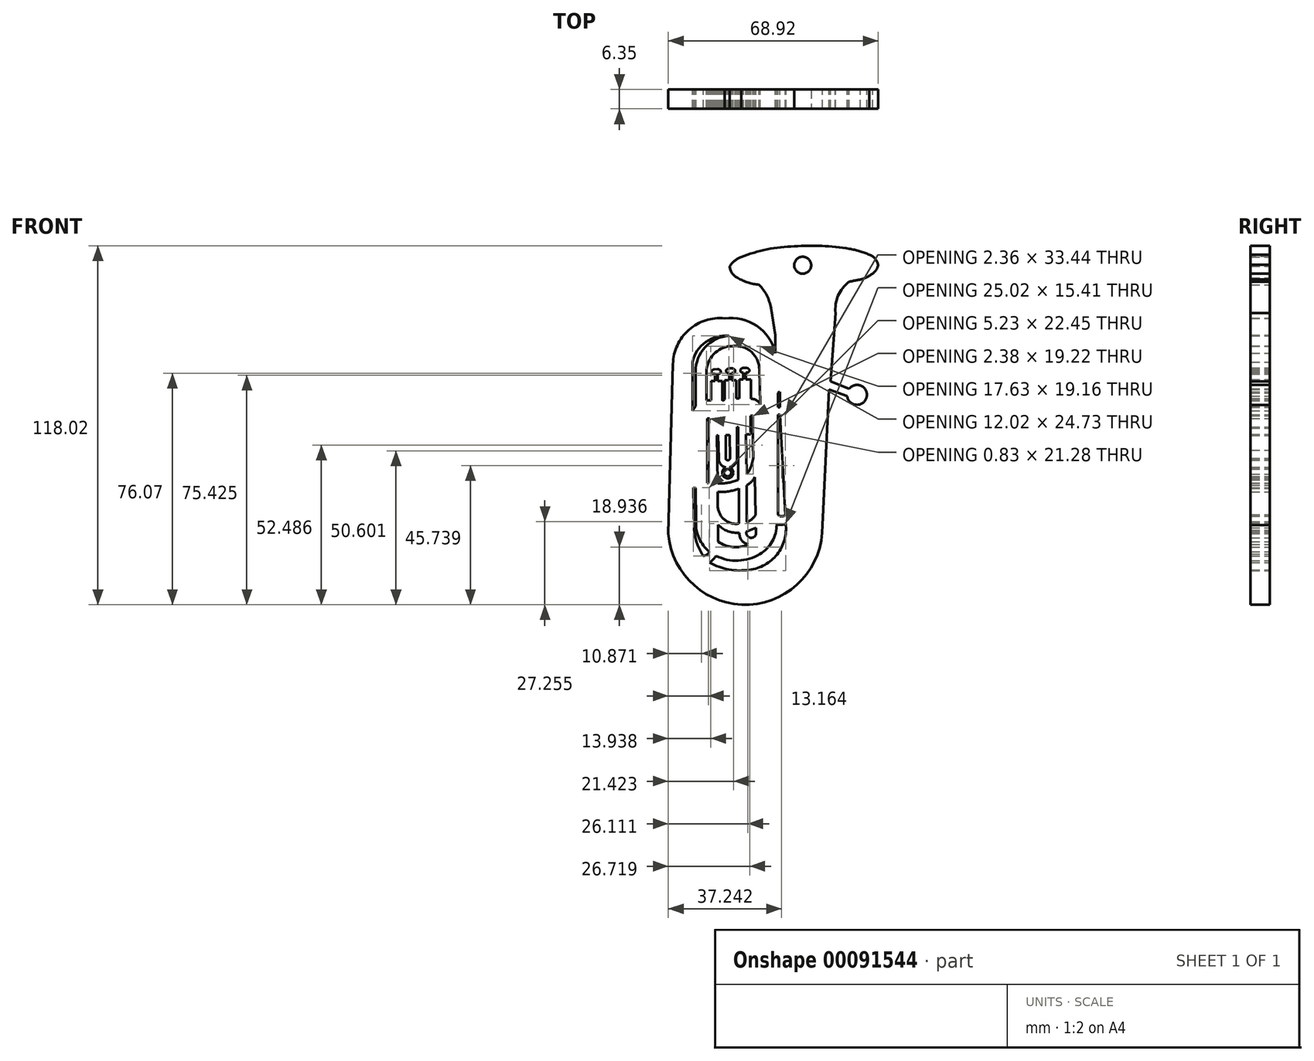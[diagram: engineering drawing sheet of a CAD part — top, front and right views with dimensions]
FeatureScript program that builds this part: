
annotation { "Feature Type Name" : "Feature", "Feature Type Description" : "" }
export const myFeature = defineFeature(function(context is Context, id is Id, definition is map)
    precondition{}
    {
        {
            var Q0;
            Q0=qCreatedBy(makeId("Front.planeOp"),FACE);
            var sketch = newSketch(context, id + "F0", { "sketchPlane" : qUnion([Q0])});
            skLineSegment(sketch, "E0", {"start": v(-26.63, 5.95) * mm, "end": v(-25.1, 61.67) * mm});
            skArc(sketch, "E1", {"start": v(-8.1, 76.7) * mm, "mid": v(-19.86, 72.87) * mm, "end": v(-25.1, 61.67) * mm});
            skArc(sketch, "E2", {"start": v(8.56, 65.28) * mm, "mid": v(2.44, 74.2) * mm, "end": v(-8.1, 76.7) * mm});
            skLineSegment(sketch, "E3", {"start": v(9.42, 52.17) * mm, "end": v(9.42, 47.42) * mm});
            skLineSegment(sketch, "E4", {"start": v(9.42, 47.42) * mm, "end": v(10.08, 47.42) * mm});
            skLineSegment(sketch, "E5", {"start": v(10.08, 47.42) * mm, "end": v(10.08, 52.5) * mm});
            skLineSegment(sketch, "E6", {"start": v(10.08, 52.5) * mm, "end": v(9.42, 52.17) * mm});
            skLineSegment(sketch, "E7", {"start": v(9.43, 45) * mm, "end": v(9.43, 12.17) * mm});
            skLineSegment(sketch, "E8", {"start": v(9.43, 45) * mm, "end": v(10.02, 45) * mm});
            skLineSegment(sketch, "E9", {"start": v(10.02, 45) * mm, "end": v(11.8, 12) * mm});
            skArc(sketch, "E10", {"start": v(9.43, 12.17) * mm, "mid": v(10.58, 11.57) * mm, "end": v(11.8, 12) * mm});
            skArc(sketch, "E11", {"start": v(0, -6) * mm, "mid": v(9.13, -0.89) * mm, "end": v(11.92, 9.2) * mm});
            skArc(sketch, "E12", {"start": v(-13.03, -3.63) * mm, "mid": v(-6.71, -5.9) * mm, "end": v(0, -6) * mm});
            skArc(sketch, "E13", {"start": v(-13.03, -3.63) * mm, "mid": v(-11.87, -2.63) * mm, "end": v(-10.93, -1.4) * mm});
            skArc(sketch, "E14", {"start": v(-10.93, -1.4) * mm, "mid": v(-3.67, -2.98) * mm, "end": v(3.43, -0.81) * mm});
            skArc(sketch, "E15", {"start": v(3.43, -0.81) * mm, "mid": v(7.54, 3.34) * mm, "end": v(8.99, 9) * mm});
            skArc(sketch, "E16", {"start": v(8.99, 9) * mm, "mid": v(10.47, 8.8) * mm, "end": v(11.92, 9.2) * mm});
            skArc(sketch, "E17", {"start": v(-15.12, -1.42) * mm, "mid": v(-13.94, -0.98) * mm, "end": v(-13.14, 0) * mm});
            skArc(sketch, "E18", {"start": v(-17.53, 9.9) * mm, "mid": v(-16.54, 4.41) * mm, "end": v(-13.14, 0) * mm});
            skArc(sketch, "E19", {"start": v(-18.1, 7.06) * mm, "mid": v(-17.15, 2.63) * mm, "end": v(-15.12, -1.42) * mm});
            skLineSegment(sketch, "E20", {"start": v(-18.1, 7.06) * mm, "end": v(-18.37, 21.03) * mm});
            skLineSegment(sketch, "E21", {"start": v(-18.37, 21.03) * mm, "end": v(-17.63, 20.86) * mm});
            skLineSegment(sketch, "E22", {"start": v(-17.63, 20.86) * mm, "end": v(-17.53, 9.9) * mm});
            skArc(sketch, "E23", {"start": v(-26.63, 5.95) * mm, "mid": v(0.02, -17.4) * mm, "end": v(23.97, 8.72) * mm});
            skLineSegment(sketch, "E24", {"start": v(23.97, 8.72) * mm, "end": v(26.22, 53.25) * mm});
            skLineSegment(sketch, "E25", {"start": v(26.22, 53.25) * mm, "end": v(32.11, 51.17) * mm});
            skArc(sketch, "E26", {"start": v(32.11, 51.17) * mm, "mid": v(38.5, 50.6) * mm, "end": v(32.8, 53.55) * mm});
            skLineSegment(sketch, "E27", {"start": v(32.8, 53.55) * mm, "end": v(26.63, 55.95) * mm});
            skLineSegment(sketch, "E28", {"start": v(26.63, 55.95) * mm, "end": v(28.3, 78.4) * mm});
            skArc(sketch, "E29", {"start": v(32.7, 88.67) * mm, "mid": v(29.16, 84.1) * mm, "end": v(28.3, 78.4) * mm});
            skArc(sketch, "E30", {"start": v(-10.24, 3.22) * mm, "mid": v(-5.44, 1.5) * mm, "end": v(-0.4, 2.37) * mm});
            skLineSegment(sketch, "E31", {"start": v(-10.24, 3.22) * mm, "end": v(-10.24, 8.8) * mm});
            skArc(sketch, "E32", {"start": v(-10.24, 8.8) * mm, "mid": v(-7.05, 6.72) * mm, "end": v(-3.27, 6.21) * mm});
            skArc(sketch, "E33", {"start": v(-3.27, 6.21) * mm, "mid": v(-2.57, 3.75) * mm, "end": v(-0.4, 2.37) * mm});
            skArc(sketch, "E34", {"start": v(-0.95, 6.52) * mm, "mid": v(0.31, 4.55) * mm, "end": v(2.23, 5.9) * mm});
            skLineSegment(sketch, "E35", {"start": v(-0.95, 6.52) * mm, "end": v(2.14, 7.78) * mm});
            skLineSegment(sketch, "E36", {"start": v(2.14, 7.78) * mm, "end": v(2.23, 5.9) * mm});
            skLineSegment(sketch, "E37", {"start": v(-10.37, 19.62) * mm, "end": v(-10.37, 15.15) * mm});
            skArc(sketch, "E38", {"start": v(-10.37, 15.15) * mm, "mid": v(-8.26, 10.57) * mm, "end": v(-3.4, 9.2) * mm});
            skLineSegment(sketch, "E39", {"start": v(-3.4, 9.2) * mm, "end": v(-3.4, 20.73) * mm});
            skArc(sketch, "E40", {"start": v(-10.37, 19.62) * mm, "mid": v(-6.83, 19.78) * mm, "end": v(-3.4, 20.73) * mm});
            skArc(sketch, "E41", {"start": v(-0.86, 9.7) * mm, "mid": v(0.8, 10.63) * mm, "end": v(2.05, 12.07) * mm});
            skLineSegment(sketch, "E42", {"start": v(-0.86, 9.7) * mm, "end": v(-0.86, 21.76) * mm});
            skArc(sketch, "E43", {"start": v(-0.86, 21.76) * mm, "mid": v(0.65, 22.96) * mm, "end": v(1.84, 24.47) * mm});
            skLineSegment(sketch, "E44", {"start": v(1.84, 24.47) * mm, "end": v(2.05, 12.07) * mm});
            skLineSegment(sketch, "E45", {"start": v(-10.7, 38.17) * mm, "end": v(-10.38, 22.43) * mm});
            skArc(sketch, "E46", {"start": v(-10.38, 22.43) * mm, "mid": v(-6.93, 22.63) * mm, "end": v(-3.63, 23.62) * mm});
            skLineSegment(sketch, "E47", {"start": v(-3.63, 23.62) * mm, "end": v(-3.63, 40.94) * mm});
            skLineSegment(sketch, "E48", {"start": v(-3.63, 40.94) * mm, "end": v(-4.03, 40.94) * mm});
            skLineSegment(sketch, "E49", {"start": v(-4.03, 40.94) * mm, "end": v(-4.03, 30.64) * mm});
            skArc(sketch, "E50", {"start": v(-6.6, 27.7) * mm, "mid": v(-4.76, 28.69) * mm, "end": v(-4.03, 30.64) * mm});
            skCircle(sketch, "E51", {"center": v(-7.15, 25.95) * mm, "radius": 1.18 * mm});
            skArc(sketch, "E52", {"start": v(-7.06, 24.09) * mm, "mid": v(-5.26, 25.7) * mm, "end": v(-6.6, 27.7) * mm});
            skArc(sketch, "E53", {"start": v(-7.67, 27.64) * mm, "mid": v(-8.88, 25.6) * mm, "end": v(-7.06, 24.09) * mm});
            skArc(sketch, "E54", {"start": v(-10.06, 30.55) * mm, "mid": v(-9.38, 28.67) * mm, "end": v(-7.67, 27.64) * mm});
            skLineSegment(sketch, "E55", {"start": v(-10.06, 30.55) * mm, "end": v(-10.22, 38.24) * mm});
            skLineSegment(sketch, "E56", {"start": v(-10.22, 38.24) * mm, "end": v(-10.7, 38.17) * mm});
            skArc(sketch, "E57", {"start": v(-0.88, 25.42) * mm, "mid": v(0.96, 29.16) * mm, "end": v(1.17, 33.32) * mm});
            skLineSegment(sketch, "E58", {"start": v(1.17, 33.32) * mm, "end": v(1.17, 44.65) * mm});
            skLineSegment(sketch, "E59", {"start": v(1.17, 44.65) * mm, "end": v(0.37, 44.65) * mm});
            skLineSegment(sketch, "E60", {"start": v(0.37, 44.65) * mm, "end": v(0.37, 38.54) * mm});
            skLineSegment(sketch, "E61", {"start": v(0.37, 38.54) * mm, "end": v(-1.1, 38.54) * mm});
            skLineSegment(sketch, "E62", {"start": v(-1.1, 38.54) * mm, "end": v(-0.88, 25.42) * mm});
            skArc(sketch, "E63", {"start": v(-7.8, 30.64) * mm, "mid": v(-7.08, 30.01) * mm, "end": v(-6.37, 30.64) * mm});
            skLineSegment(sketch, "E64", {"start": v(-7.8, 30.64) * mm, "end": v(-7.8, 38.28) * mm});
            skLineSegment(sketch, "E65", {"start": v(-7.8, 38.28) * mm, "end": v(-6.43, 38.28) * mm});
            skLineSegment(sketch, "E66", {"start": v(-6.43, 38.28) * mm, "end": v(-6.37, 30.64) * mm});
            skLineSegment(sketch, "E67", {"start": v(-13.88, 22.59) * mm, "end": v(-13.88, 43.8) * mm});
            skLineSegment(sketch, "E68", {"start": v(-13.88, 43.8) * mm, "end": v(-13.05, 43.8) * mm});
            skLineSegment(sketch, "E69", {"start": v(-13.05, 43.8) * mm, "end": v(-13.47, 40.57) * mm});
            skLineSegment(sketch, "E70", {"start": v(-13.47, 40.57) * mm, "end": v(-13.47, 22.5) * mm});
            skLineSegment(sketch, "E71", {"start": v(-13.47, 22.5) * mm, "end": v(-13.88, 22.59) * mm});
            skLineSegment(sketch, "E72", {"start": v(-18.7, 46.26) * mm, "end": v(-18.7, 62.35) * mm});
            skArc(sketch, "E73", {"start": v(-6.68, 70.97) * mm, "mid": v(-14.31, 68.92) * mm, "end": v(-18.7, 62.35) * mm});
            skArc(sketch, "E74", {"start": v(-6.68, 70.97) * mm, "mid": v(-14.5, 67.22) * mm, "end": v(-17.67, 59.16) * mm});
            skLineSegment(sketch, "E75", {"start": v(-17.67, 59.16) * mm, "end": v(-17.67, 47.8) * mm});
            skLineSegment(sketch, "E76", {"start": v(-17.67, 47.8) * mm, "end": v(-18.7, 46.26) * mm});
            skLineSegment(sketch, "E77", {"start": v(-14.02, 49.69) * mm, "end": v(-12.62, 49.69) * mm});
            skLineSegment(sketch, "E78", {"start": v(-12.62, 49.69) * mm, "end": v(-12.62, 56.06) * mm});
            skLineSegment(sketch, "E79", {"start": v(-12.62, 56.06) * mm, "end": v(-11.34, 56.06) * mm});
            skLineSegment(sketch, "E80", {"start": v(-11.34, 56.06) * mm, "end": v(-11.34, 58.34) * mm});
            skLineSegment(sketch, "E81", {"start": v(-14.02, 49.69) * mm, "end": v(-14.02, 59.75) * mm});
            skArc(sketch, "E82", {"start": v(-5.25, 67.55) * mm, "mid": v(-11.2, 65.41) * mm, "end": v(-14.02, 59.75) * mm});
            skArc(sketch, "E83", {"start": v(3.26, 60.1) * mm, "mid": v(0.63, 65.69) * mm, "end": v(-5.25, 67.55) * mm});
            skLineSegment(sketch, "E84", {"start": v(3.26, 60.1) * mm, "end": v(3.61, 48.4) * mm});
            skArc(sketch, "E85", {"start": v(3.61, 48.4) * mm, "mid": v(2.35, 49.77) * mm, "end": v(0.53, 50.2) * mm});
            skLineSegment(sketch, "E86", {"start": v(0.53, 50.2) * mm, "end": v(0.53, 56.55) * mm});
            skLineSegment(sketch, "E87", {"start": v(0.53, 56.55) * mm, "end": v(-1.07, 56.55) * mm});
            skLineSegment(sketch, "E88", {"start": v(-1.07, 56.55) * mm, "end": v(-1.07, 58.77) * mm});
            skLineSegment(sketch, "E89", {"start": v(-10.41, 58.42) * mm, "end": v(-10.41, 56.07) * mm});
            skLineSegment(sketch, "E90", {"start": v(-10.41, 56.07) * mm, "end": v(-8.9, 56.07) * mm});
            skLineSegment(sketch, "E91", {"start": v(-8.9, 56.07) * mm, "end": v(-8.9, 49.55) * mm});
            skLineSegment(sketch, "E92", {"start": v(-8.9, 49.55) * mm, "end": v(-8.07, 50.02) * mm});
            skLineSegment(sketch, "E93", {"start": v(-8.07, 50.02) * mm, "end": v(-8.07, 56.28) * mm});
            skLineSegment(sketch, "E94", {"start": v(-8.07, 56.28) * mm, "end": v(-6.62, 56.28) * mm});
            skLineSegment(sketch, "E95", {"start": v(-6.62, 56.28) * mm, "end": v(-6.62, 58.8) * mm});
            skLineSegment(sketch, "E96", {"start": v(-7.65, 59.13) * mm, "end": v(-7.65, 59.67) * mm});
            skArc(sketch, "E97", {"start": v(-6.12, 60.26) * mm, "mid": v(-6.96, 60.15) * mm, "end": v(-7.65, 59.67) * mm});
            skArc(sketch, "E98", {"start": v(-4.64, 59.63) * mm, "mid": v(-5.3, 60.13) * mm, "end": v(-6.12, 60.26) * mm});
            skLineSegment(sketch, "E99", {"start": v(-4.64, 59.63) * mm, "end": v(-4.64, 59.14) * mm});
            skArc(sketch, "E100", {"start": v(-5.42, 58.69) * mm, "mid": v(-4.96, 58.8) * mm, "end": v(-4.64, 59.14) * mm});
            skLineSegment(sketch, "E101", {"start": v(-5.42, 58.69) * mm, "end": v(-5.78, 58.7) * mm});
            skLineSegment(sketch, "E102", {"start": v(-5.78, 58.7) * mm, "end": v(-5.78, 56.3) * mm});
            skLineSegment(sketch, "E103", {"start": v(-5.78, 56.3) * mm, "end": v(-4.26, 56.3) * mm});
            skLineSegment(sketch, "E104", {"start": v(-4.26, 56.3) * mm, "end": v(-4.26, 50.3) * mm});
            skLineSegment(sketch, "E105", {"start": v(-4.26, 50.3) * mm, "end": v(-3.26, 50.3) * mm});
            skLineSegment(sketch, "E106", {"start": v(-3.26, 50.3) * mm, "end": v(-3.26, 56.55) * mm});
            skLineSegment(sketch, "E107", {"start": v(-3.26, 56.55) * mm, "end": v(-2.03, 56.55) * mm});
            skLineSegment(sketch, "E108", {"start": v(-2.03, 56.55) * mm, "end": v(-2.03, 58.92) * mm});
            skLineSegment(sketch, "E109", {"start": v(-2.03, 58.92) * mm, "end": v(-2.48, 58.92) * mm});
            skArc(sketch, "E110", {"start": v(-2.94, 59.32) * mm, "mid": v(-2.78, 59.03) * mm, "end": v(-2.48, 58.92) * mm});
            skLineSegment(sketch, "E111", {"start": v(-2.94, 59.32) * mm, "end": v(-2.94, 59.8) * mm});
            skArc(sketch, "E112", {"start": v(-1.91, 60.4) * mm, "mid": v(-2.5, 60.22) * mm, "end": v(-2.94, 59.8) * mm});
            skLineSegment(sketch, "E113", {"start": v(-1.91, 60.4) * mm, "end": v(-1.12, 60.4) * mm});
            skArc(sketch, "E114", {"start": v(0, 59.82) * mm, "mid": v(-0.49, 60.25) * mm, "end": v(-1.12, 60.4) * mm});
            skLineSegment(sketch, "E115", {"start": v(0, 59.82) * mm, "end": v(0, 59.38) * mm});
            skArc(sketch, "E116", {"start": v(-0.64, 58.89) * mm, "mid": v(-0.24, 59.02) * mm, "end": v(0, 59.38) * mm});
            skLineSegment(sketch, "E117", {"start": v(-0.64, 58.89) * mm, "end": v(-1.09, 58.9) * mm});
            skLineSegment(sketch, "E118", {"start": v(-1.09, 58.9) * mm, "end": v(-1.07, 58.77) * mm});
            skArc(sketch, "E119", {"start": v(-7.65, 59.13) * mm, "mid": v(-7.46, 58.85) * mm, "end": v(-7.15, 58.7) * mm});
            skLineSegment(sketch, "E120", {"start": v(-7.15, 58.7) * mm, "end": v(-6.62, 58.7) * mm});
            skLineSegment(sketch, "E121", {"start": v(-11.34, 58.34) * mm, "end": v(-11.34, 58.46) * mm});
            skLineSegment(sketch, "E122", {"start": v(-11.34, 58.46) * mm, "end": v(-11.87, 58.46) * mm});
            skArc(sketch, "E123", {"start": v(-12.38, 58.88) * mm, "mid": v(-12.16, 58.62) * mm, "end": v(-11.87, 58.46) * mm});
            skLineSegment(sketch, "E124", {"start": v(-12.38, 58.88) * mm, "end": v(-12.38, 59.38) * mm});
            skArc(sketch, "E125", {"start": v(-11.51, 59.94) * mm, "mid": v(-12, 59.76) * mm, "end": v(-12.38, 59.38) * mm});
            skLineSegment(sketch, "E126", {"start": v(-11.51, 59.94) * mm, "end": v(-10.35, 59.98) * mm});
            skArc(sketch, "E127", {"start": v(-9.38, 59.35) * mm, "mid": v(-9.79, 59.78) * mm, "end": v(-10.35, 59.98) * mm});
            skLineSegment(sketch, "E128", {"start": v(-9.38, 59.35) * mm, "end": v(-9.38, 58.93) * mm});
            skArc(sketch, "E129", {"start": v(-9.93, 58.48) * mm, "mid": v(-9.59, 58.62) * mm, "end": v(-9.38, 58.93) * mm});
            skLineSegment(sketch, "E130", {"start": v(-10.41, 58.42) * mm, "end": v(-9.93, 58.48) * mm});
            skLineSegment(sketch, "E131", {"start": v(8.56, 65.28) * mm, "end": v(8.56, 71.25) * mm});
            skLineSegment(sketch, "E132", {"start": v(8.56, 71.25) * mm, "end": v(7.08, 80.13) * mm});
            skArc(sketch, "E133", {"start": v(7.08, 80.13) * mm, "mid": v(5.72, 84.25) * mm, "end": v(3.18, 87.75) * mm});
            skArc(sketch, "E134", {"start": v(-3.8, 89.93) * mm, "mid": v(-0.42, 88.46) * mm, "end": v(3.18, 87.75) * mm});
            skArc(sketch, "E135", {"start": v(-6.43, 93.83) * mm, "mid": v(-5.64, 91.52) * mm, "end": v(-3.8, 89.93) * mm});
            skArc(sketch, "E136", {"start": v(14.78, 100.36) * mm, "mid": v(5.87, 99.38) * mm, "end": v(-2.71, 96.82) * mm});
            skArc(sketch, "E137", {"start": v(32.85, 99.56) * mm, "mid": v(23.84, 100.5) * mm, "end": v(14.78, 100.36) * mm});
            skArc(sketch, "E138", {"start": v(-2.71, 96.82) * mm, "mid": v(-4.81, 95.62) * mm, "end": v(-6.43, 93.83) * mm});
            skArc(sketch, "E139", {"start": v(39.45, 97.63) * mm, "mid": v(36.2, 98.78) * mm, "end": v(32.85, 99.56) * mm});
            skArc(sketch, "E140", {"start": v(42.29, 94.27) * mm, "mid": v(41.3, 96.32) * mm, "end": v(39.45, 97.63) * mm});
            skArc(sketch, "E141", {"start": v(40.47, 91.43) * mm, "mid": v(41.72, 92.63) * mm, "end": v(42.29, 94.27) * mm});
            skArc(sketch, "E142", {"start": v(36.43, 89.44) * mm, "mid": v(38.57, 90.2) * mm, "end": v(40.47, 91.43) * mm});
            skArc(sketch, "E143", {"start": v(36.43, 89.44) * mm, "mid": v(34.57, 89.08) * mm, "end": v(32.7, 88.67) * mm});
            skSolve(sketch);
        }
        {
            var Q0;
            Q0=makeQuery(id+"F0.imprint","IMPRINT",FACE,{"disambiguationData":[TD([[makeQuery(id+"F0.imprint","IMPRINT",EDGE,{"derivedFrom":sQuery(id+"F0.wireOp",EDGE,"E0")}),-1.0]])]});
            extrude(context, id + "F1", {"entities" : qUnion([Q0]), "depth" : 6.35 * mm});
        }
        {
            var Q0;
            Q0=makeQuery(id+"F1.opExtrude","CAP_FACE",FACE,{"disambiguationData":[OSD([sQuery(id+"F0.wireOp",EDGE,"E0"),sQuery(id+"F0.wireOp",EDGE,"E1"),sQuery(id+"F0.wireOp",EDGE,"E2"),sQuery(id+"F0.wireOp",EDGE,"E3"),sQuery(id+"F0.wireOp",EDGE,"E4"),sQuery(id+"F0.wireOp",EDGE,"E5"),sQuery(id+"F0.wireOp",EDGE,"E6"),sQuery(id+"F0.wireOp",EDGE,"E7"),sQuery(id+"F0.wireOp",EDGE,"E8"),sQuery(id+"F0.wireOp",EDGE,"E9"),sQuery(id+"F0.wireOp",EDGE,"E10"),sQuery(id+"F0.wireOp",EDGE,"E11"),sQuery(id+"F0.wireOp",EDGE,"E12"),sQuery(id+"F0.wireOp",EDGE,"E13"),sQuery(id+"F0.wireOp",EDGE,"E14"),sQuery(id+"F0.wireOp",EDGE,"E15"),sQuery(id+"F0.wireOp",EDGE,"E16"),sQuery(id+"F0.wireOp",EDGE,"E17"),sQuery(id+"F0.wireOp",EDGE,"E18"),sQuery(id+"F0.wireOp",EDGE,"E19"),sQuery(id+"F0.wireOp",EDGE,"E20"),sQuery(id+"F0.wireOp",EDGE,"E21"),sQuery(id+"F0.wireOp",EDGE,"E22"),sQuery(id+"F0.wireOp",EDGE,"E23"),sQuery(id+"F0.wireOp",EDGE,"E24"),sQuery(id+"F0.wireOp",EDGE,"E25"),sQuery(id+"F0.wireOp",EDGE,"E26"),sQuery(id+"F0.wireOp",EDGE,"E27"),sQuery(id+"F0.wireOp",EDGE,"E28"),sQuery(id+"F0.wireOp",EDGE,"E29"),sQuery(id+"F0.wireOp",EDGE,"E30"),sQuery(id+"F0.wireOp",EDGE,"E31"),sQuery(id+"F0.wireOp",EDGE,"E32"),sQuery(id+"F0.wireOp",EDGE,"E33"),sQuery(id+"F0.wireOp",EDGE,"E34"),sQuery(id+"F0.wireOp",EDGE,"E35"),sQuery(id+"F0.wireOp",EDGE,"E36"),sQuery(id+"F0.wireOp",EDGE,"E37"),sQuery(id+"F0.wireOp",EDGE,"E38"),sQuery(id+"F0.wireOp",EDGE,"E39"),sQuery(id+"F0.wireOp",EDGE,"E40"),sQuery(id+"F0.wireOp",EDGE,"E41"),sQuery(id+"F0.wireOp",EDGE,"E42"),sQuery(id+"F0.wireOp",EDGE,"E43"),sQuery(id+"F0.wireOp",EDGE,"E44"),sQuery(id+"F0.wireOp",EDGE,"E45"),sQuery(id+"F0.wireOp",EDGE,"E46"),sQuery(id+"F0.wireOp",EDGE,"E47"),sQuery(id+"F0.wireOp",EDGE,"E48"),sQuery(id+"F0.wireOp",EDGE,"E49"),sQuery(id+"F0.wireOp",EDGE,"E50"),sQuery(id+"F0.wireOp",EDGE,"E51"),sQuery(id+"F0.wireOp",EDGE,"E52"),sQuery(id+"F0.wireOp",EDGE,"E53"),sQuery(id+"F0.wireOp",EDGE,"E54"),sQuery(id+"F0.wireOp",EDGE,"E55"),sQuery(id+"F0.wireOp",EDGE,"E56"),sQuery(id+"F0.wireOp",EDGE,"E57"),sQuery(id+"F0.wireOp",EDGE,"E58"),sQuery(id+"F0.wireOp",EDGE,"E59"),sQuery(id+"F0.wireOp",EDGE,"E60"),sQuery(id+"F0.wireOp",EDGE,"E61"),sQuery(id+"F0.wireOp",EDGE,"E62"),sQuery(id+"F0.wireOp",EDGE,"E63"),sQuery(id+"F0.wireOp",EDGE,"E64"),sQuery(id+"F0.wireOp",EDGE,"E65"),sQuery(id+"F0.wireOp",EDGE,"E66"),sQuery(id+"F0.wireOp",EDGE,"E67"),sQuery(id+"F0.wireOp",EDGE,"E68"),sQuery(id+"F0.wireOp",EDGE,"E69"),sQuery(id+"F0.wireOp",EDGE,"E70"),sQuery(id+"F0.wireOp",EDGE,"E71"),sQuery(id+"F0.wireOp",EDGE,"E72"),sQuery(id+"F0.wireOp",EDGE,"E73"),sQuery(id+"F0.wireOp",EDGE,"E74"),sQuery(id+"F0.wireOp",EDGE,"E75"),sQuery(id+"F0.wireOp",EDGE,"E76"),sQuery(id+"F0.wireOp",EDGE,"E77"),sQuery(id+"F0.wireOp",EDGE,"E78"),sQuery(id+"F0.wireOp",EDGE,"E79"),sQuery(id+"F0.wireOp",EDGE,"E80"),sQuery(id+"F0.wireOp",EDGE,"E81"),sQuery(id+"F0.wireOp",EDGE,"E82"),sQuery(id+"F0.wireOp",EDGE,"E83"),sQuery(id+"F0.wireOp",EDGE,"E84"),sQuery(id+"F0.wireOp",EDGE,"E85"),sQuery(id+"F0.wireOp",EDGE,"E86"),sQuery(id+"F0.wireOp",EDGE,"E87"),sQuery(id+"F0.wireOp",EDGE,"E88"),sQuery(id+"F0.wireOp",EDGE,"E89"),sQuery(id+"F0.wireOp",EDGE,"E90"),sQuery(id+"F0.wireOp",EDGE,"E91"),sQuery(id+"F0.wireOp",EDGE,"E92"),sQuery(id+"F0.wireOp",EDGE,"E93"),sQuery(id+"F0.wireOp",EDGE,"E94"),sQuery(id+"F0.wireOp",EDGE,"E95"),sQuery(id+"F0.wireOp",EDGE,"E96"),sQuery(id+"F0.wireOp",EDGE,"E97"),sQuery(id+"F0.wireOp",EDGE,"E98"),sQuery(id+"F0.wireOp",EDGE,"E99"),sQuery(id+"F0.wireOp",EDGE,"E100"),sQuery(id+"F0.wireOp",EDGE,"E101"),sQuery(id+"F0.wireOp",EDGE,"E102"),sQuery(id+"F0.wireOp",EDGE,"E103"),sQuery(id+"F0.wireOp",EDGE,"E104"),sQuery(id+"F0.wireOp",EDGE,"E105"),sQuery(id+"F0.wireOp",EDGE,"E106"),sQuery(id+"F0.wireOp",EDGE,"E107"),sQuery(id+"F0.wireOp",EDGE,"E108"),sQuery(id+"F0.wireOp",EDGE,"E109"),sQuery(id+"F0.wireOp",EDGE,"E110"),sQuery(id+"F0.wireOp",EDGE,"E111"),sQuery(id+"F0.wireOp",EDGE,"E112"),sQuery(id+"F0.wireOp",EDGE,"E113"),sQuery(id+"F0.wireOp",EDGE,"E114"),sQuery(id+"F0.wireOp",EDGE,"E115"),sQuery(id+"F0.wireOp",EDGE,"E116"),sQuery(id+"F0.wireOp",EDGE,"E117"),sQuery(id+"F0.wireOp",EDGE,"E118"),sQuery(id+"F0.wireOp",EDGE,"E119"),sQuery(id+"F0.wireOp",EDGE,"E120"),sQuery(id+"F0.wireOp",EDGE,"E121"),sQuery(id+"F0.wireOp",EDGE,"E122"),sQuery(id+"F0.wireOp",EDGE,"E123"),sQuery(id+"F0.wireOp",EDGE,"E124"),sQuery(id+"F0.wireOp",EDGE,"E125"),sQuery(id+"F0.wireOp",EDGE,"E126"),sQuery(id+"F0.wireOp",EDGE,"E127"),sQuery(id+"F0.wireOp",EDGE,"E128"),sQuery(id+"F0.wireOp",EDGE,"E129"),sQuery(id+"F0.wireOp",EDGE,"E130"),sQuery(id+"F0.wireOp",EDGE,"E131"),sQuery(id+"F0.wireOp",EDGE,"E132"),sQuery(id+"F0.wireOp",EDGE,"E133"),sQuery(id+"F0.wireOp",EDGE,"E134"),sQuery(id+"F0.wireOp",EDGE,"E135"),sQuery(id+"F0.wireOp",EDGE,"E136"),sQuery(id+"F0.wireOp",EDGE,"E137"),sQuery(id+"F0.wireOp",EDGE,"E138"),sQuery(id+"F0.wireOp",EDGE,"E139"),sQuery(id+"F0.wireOp",EDGE,"E140"),sQuery(id+"F0.wireOp",EDGE,"E141"),sQuery(id+"F0.wireOp",EDGE,"E142"),sQuery(id+"F0.wireOp",EDGE,"E143")])],"isStart":false});
            var sketch = newSketch(context, id + "F2", { "sketchPlane" : qUnion([Q0])});
            skCircle(sketch, "E144", {"center": v(17.53, 94.15) * mm, "radius": 2.8 * mm});
            skLineSegment(sketch, "E145", {"start": v(3.18, 87.75) * mm, "end": v(32.7, 88.67) * mm, "construction": true});
            skLineSegment(sketch, "E146", {"start": v(17.95, 88.21) * mm, "end": v(17.53, 94.15) * mm, "construction": true});
            skSolve(sketch);
        }
        {
            var Q0;
            Q0=makeQuery(id+"F2.imprint","IMPRINT",FACE,{"disambiguationData":[TD([[makeQuery(id+"F2.imprint","IMPRINT",EDGE,{"derivedFrom":sQuery(id+"F2.wireOp",EDGE,"E144")}),1.0]])]});
            extrude(context, id + "F3", {"entities" : qUnion([Q0]), "operationType" : NewBodyOperationType.REMOVE, "oppositeDirection" : true, "depth" : 25.4 * mm});
        }
    });
